# Revit family: Gunnebo_HalfHghtAcsCtrlGts_SpeedStileFLs-Max
name_source: partatom
category: Specialty Equipment
units: mm (PartAtom-declared; Revit-internal decimal feet)

## family parameters
Always vertical = Yes
Cut with Voids When Loaded = No
Part Type = Normal
Room Calculation Point = No
Round Connector Dimension = Use Diameter
Shared = No
Work Plane-Based = No

## types (16) — shared parameters
AcousticRating = Less than 55dB
ApparentLoad = 0 VA
AssetType = Fixed
BIMObjectName = Gunnebo_HalfHeightAccessControlGates_SpeedStileFLs_Max
BodyMaterial = Gunnebo_StainlessSteel
Category = Pr_30_59_34_88 | Stainless steel half height turnstiles
CentralPanelMaterial = Gunnebo_ToughenedGlass
ControlUnit = Master SpeeStile cabinet
Description = Automated boarding gates
DurationUnit = years
ExpectedLife = 10
Finish = Chassis, plinth and end leg posts and rotor column finishing in 304 grade stainless steel and glass inlay 10mm thick. Standard finish for lid: Black technopolymer (square ends).
FireExit = No
Frosted Light Strip Option3 = Ambient + Dynamic Lights with Enhanced Audio
GateType = Flap Wings
GlazingAreaFraction = 0
HandicapAccesible = No
HasDrive = Yes
HasProtectiveEarth = No
IP_Code = IP 20
IfcExportAs = IfcDoorType
IfcExportType = GATE
Infiltration = 0
InstallationDate (default) = 1900-12-31T23:59:59
InsulationStandardClass = CLASSIAPPLIANCE
IsExternal = No
LEDMaterial = Gunnebo_LED_Green
LidMaterial = Gunnebo_Black
LoadClassification = Other
Manufacturer = Gunnebo Entrance Control
Manufacturer Website = https://www.gunneboentrancecontrol.com
ManufacturerName = Gunnebo
Material = 304 Grade Stainless Steel
ModelReference = SpeedStileFLs_Max
Name = SpeedStile FLs MAX
NominalFrequencyRange = 50 Hz
NominalHeight = 982
NominalLength = 1314-1534
NominalWidth = 132
NumberOfPoles = 1
Overall Height = 980 mm  [stored 3.21522 ft]
Overall Length = 1530 mm  [stored 5.01969 ft]
Overall Width = 600 mm
PowerFactor = 0
Product URL = https://www.gunneboentrancecontrol.com
ProductInformation = www.gunnebo.com
RatedVoltage = 230 V
Rotation = Two-way direction
SelfClosing = No
SmokeStop = No
Status = UNSET
ThermalTransmittance = 0
Uniclass2015Code = Pr_30_59_34_88
Uniclass2015Title = Half-Height access control gates
Uniclass2015Version = Products v1.20
Version = 1
Voltage = 230 V
WingPanelMaterial = Gunnebo_ToughenedGlass
zero-valued in all types: Default Elevation

## per-type parameters (varying)
| type | Cabinet Length | EndProfile | FLs Max Rounded Cabinet | FLs Max Square Cabinet | Has Left Panel | Has Right Panel | Left Panel Width | Left Side Cabinet | Right Panel Width | Right Side Cabinet |
| SpeedStileFLsMax_Rounded_Centre | 1532 mm  [stored 5.02625 ft] | Rounded | Yes | No | Yes | Yes | 395 mm  [stored 1.29593 ft] | No | 395 mm  [stored 1.29593 ft] | Yes |
| SpeedStileFLsMax_Rounded_CentreLeftWide | 1532 mm  [stored 5.02625 ft] | Rounded | Yes | No | Yes | Yes | 545 mm  [stored 1.78806 ft] | No | 395 mm  [stored 1.29593 ft] | No |
| SpeedStileFLsMax_Rounded_CentreRightWide | 1532 mm  [stored 5.02625 ft] | Rounded | Yes | No | Yes | Yes | 395 mm  [stored 1.29593 ft] | No | 545 mm  [stored 1.78806 ft] | No |
| SpeedStileFLsMax_Rounded_CentreWide | 1532 mm  [stored 5.02625 ft] | Rounded | Yes | No | Yes | Yes | 545 mm  [stored 1.78806 ft] | No | 545 mm  [stored 1.78806 ft] | No |
| SpeedStileFLsMax_Rounded_Left | 1532 mm  [stored 5.02625 ft] | Rounded | Yes | No | Yes | No | 395 mm  [stored 1.29593 ft] | Yes | 0 mm  [stored 0 ft] | No |
| SpeedStileFLsMax_Rounded_LeftWide | 1532 mm  [stored 5.02625 ft] | Rounded | Yes | No | Yes | No | 545 mm  [stored 1.78806 ft] | Yes | 0 mm  [stored 0 ft] | No |
| SpeedStileFLsMax_Rounded_Right | 1532 mm  [stored 5.02625 ft] | Rounded | Yes | No | No | Yes | 0 mm  [stored 0 ft] | No | 395 mm  [stored 1.29593 ft] | Yes |
| SpeedStileFLsMax_Rounded_RightWide | 1532 mm  [stored 5.02625 ft] | Rounded | Yes | No | No | Yes | 0 mm  [stored 0 ft] | No | 545 mm  [stored 1.78806 ft] | Yes |
| SpeedStileFLsMax_Square_Centre | 1315 mm  [stored 4.3143 ft] | Squared | No | Yes | Yes | Yes | 395 mm  [stored 1.29593 ft] | No | 395 mm  [stored 1.29593 ft] | No |
| SpeedStileFLsMax_Square_CentreLeftWide | 1315 mm  [stored 4.3143 ft] | Squared | No | Yes | Yes | Yes | 545 mm  [stored 1.78806 ft] | No | 395 mm  [stored 1.29593 ft] | Yes |
| SpeedStileFLsMax_Square_CentreRightWide | 1315 mm  [stored 4.3143 ft] | Squared | No | Yes | Yes | Yes | 395 mm  [stored 1.29593 ft] | No | 545 mm  [stored 1.78806 ft] | No |
| SpeedStileFLsMax_Square_CentreWide | 1315 mm  [stored 4.3143 ft] | Squared | No | Yes | Yes | Yes | 545 mm  [stored 1.78806 ft] | No | 545 mm  [stored 1.78806 ft] | No |
| SpeedStileFLsMax_Square_Left | 1315 mm  [stored 4.3143 ft] | Squared | No | Yes | Yes | No | 395 mm  [stored 1.29593 ft] | Yes | 0 mm  [stored 0 ft] | No |
| SpeedStileFLsMax_Square_LeftWide | 1315 mm  [stored 4.3143 ft] | Squared | No | Yes | Yes | No | 545 mm  [stored 1.78806 ft] | Yes | 0 mm  [stored 0 ft] | No |
| SpeedStileFLsMax_Square_Right | 1315 mm  [stored 4.3143 ft] | Squared | No | Yes | No | Yes | 0 mm  [stored 0 ft] | No | 395 mm  [stored 1.29593 ft] | Yes |
| SpeedStileFLsMax_Square_RightWide | 1315 mm  [stored 4.3143 ft] | Squared | No | Yes | No | Yes | 0 mm  [stored 0 ft] | No | 545 mm  [stored 1.78806 ft] | Yes |

note: [stored X ft] marks values corroborated as IEEE doubles in the binary element streams (Revit-internal decimal feet)

## geometry (parser evidence)
native form markers: Sweep x37
no freeform markers — native parametric forms only
